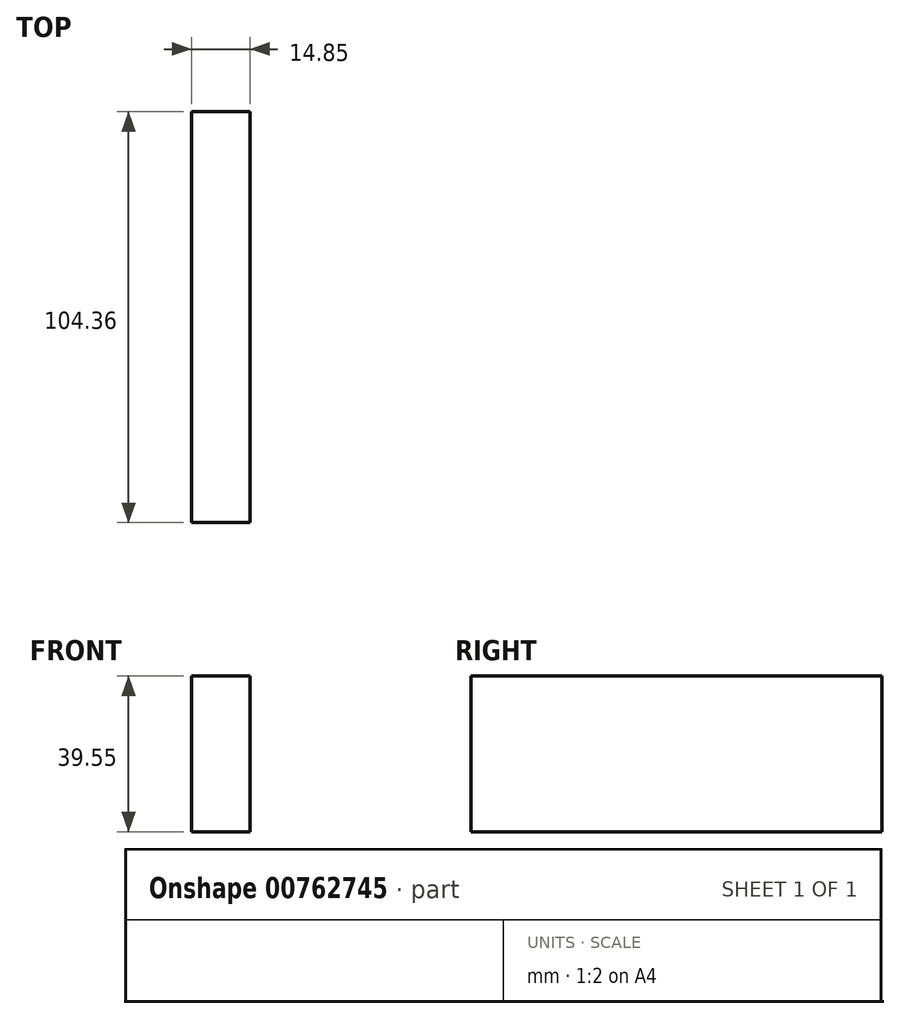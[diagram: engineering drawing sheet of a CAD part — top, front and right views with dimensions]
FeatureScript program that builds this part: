
annotation { "Feature Type Name" : "Feature", "Feature Type Description" : "" }
export const myFeature = defineFeature(function(context is Context, id is Id, definition is map)
    precondition{}
    {
        {
            var Q0;
            Q0=qCreatedBy(makeId("Front.planeOp"),FACE);
            var sketch = newSketch(context, id + "F0", { "sketchPlane" : qUnion([Q0])});
            skLineSegment(sketch, "E0.bottom", {"start": v(7.9, 25.28) * mm, "end": v(22.76, 25.28) * mm});
            skLineSegment(sketch, "E0.top", {"start": v(7.9, -14.27) * mm, "end": v(22.76, -14.27) * mm});
            skLineSegment(sketch, "E0.left", {"start": v(7.9, 25.28) * mm, "end": v(7.9, -14.27) * mm});
            skLineSegment(sketch, "E0.right", {"start": v(22.76, 25.28) * mm, "end": v(22.76, -14.27) * mm});
            skSolve(sketch);
        }
        {
            var Q0;
            Q0=makeQuery(id+"F0.imprint","IMPRINT",FACE,{"disambiguationData":[TD([[makeQuery(id+"F0.imprint","IMPRINT",EDGE,{"derivedFrom":sQuery(id+"F0.wireOp",EDGE,"E0.bottom")}),-1.0]])]});
            var Q1;
            Q1 = qSketchRegion(id + "F0", true);
            extrude(context, id + "F1", {"entities" : qUnion([Q0, Q1]), "depth" : 104.36 * mm, "offsetDistance" : 25.4 * mm});
        }
    });
